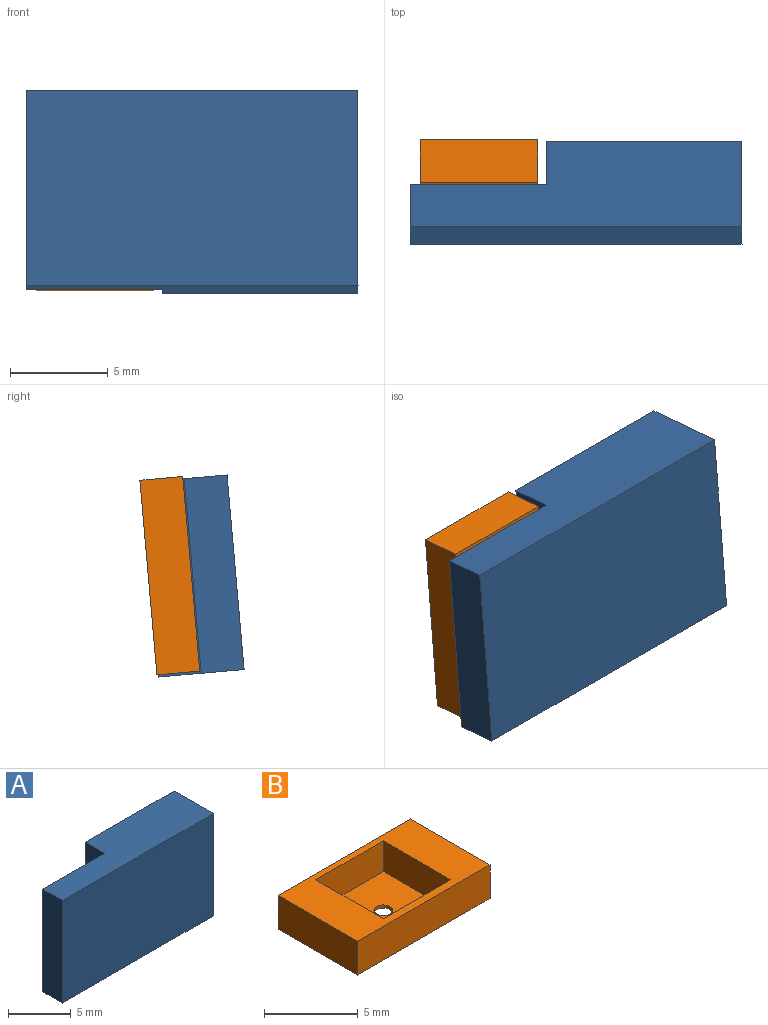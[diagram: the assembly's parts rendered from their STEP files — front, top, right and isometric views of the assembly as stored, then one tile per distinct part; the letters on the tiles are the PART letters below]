
ASSEMBLY  parts=2 mates=1
PART A: 13 faces, bbox 17x4.4x10 mm
  f0: plane 10x7mm, normal (0,1,0), area 44mm2, adj f1,f5,f6,f7,f8,f9,f10,f11
  f1: plane 10x2.2mm, normal (-1,0,0), area 22mm2, adj f0,f2,f6,f7
  f2: plane 17x10mm, normal (0,-1,0), area 170mm2, adj f1,f3,f6,f7
  f3: plane 10x4.4mm, normal (1,0,0), area 44mm2, adj f2,f4,f6,f7
  f4: plane 10x10mm, normal (0,1,0), area 100mm2, adj f3,f5,f6,f7
  f5: plane 10x2.2mm, normal (-1,0,0), area 22mm2, adj f0,f4,f6,f7
  f6: plane 17x4.4mm, normal (0,0,-1), area 59.4mm2, adj f0,f1,f2,f3,f4,f5
  f7: plane 17x4.4mm, normal (0,0,1), area 59.4mm2, adj f0,f1,f2,f3,f4,f5
  f8: plane 5.1x2mm, normal (0,0,-1), area 10.2mm2, adj f0,f9,f11,f12
  f9: plane 5.1x2mm, normal (-1,0,0), area 10.2mm2, adj f0,f8,f10,f12
  f10: plane 5.1x2mm, normal (0,0,1), area 10.2mm2, adj f0,f9,f11,f12
  f11: plane 5.1x2mm, normal (1,0,0), area 10.2mm2, adj f0,f8,f10,f12
  f12: plane 5.1x5.1mm, normal (0,1,0), area 26mm2, adj f8,f9,f10,f11
PART B: 12 faces, bbox 10x6x2.2 mm
  f0: plane 10x6mm, normal (0,0,1), area 34mm2, adj f1,f2,f3,f4,f6,f7,f8,f9
  f1: plane 6x2.2mm, normal (-1,0,0), area 13.2mm2, adj f0,f2,f4,f5
  f2: plane 10x2.2mm, normal (0,-1,0), area 22mm2, adj f0,f1,f3,f5
  f3: plane 6x2.2mm, normal (1,0,0), area 13.2mm2, adj f0,f2,f4,f5
  f4: plane 10x2.2mm, normal (0,1,0), area 22mm2, adj f0,f1,f3,f5
  f5: plane 10x6mm, normal (0,0,-1), area 59.2mm2, adj f1,f2,f3,f4,f11
  f6: plane 5.1x2mm, normal (1,0,0), area 10.2mm2, adj f0,f7,f9,f10
  f7: plane 5.1x2mm, normal (0,1,0), area 10.2mm2, adj f0,f6,f8,f10
  f8: plane 5.1x2mm, normal (-1,0,0), area 10.2mm2, adj f0,f7,f9,f10
  f9: plane 5.1x2mm, normal (0,-1,0), area 10.2mm2, adj f0,f6,f8,f10
  f10: plane 5.1x5.1mm, normal (0,0,1), area 25.2mm2, adj f6,f7,f8,f9,f11
  f11: cylinder r=0.5mm len=1mm, axis (0,0,1), area 0.6mm2, adj f5,f10
PLACE A rot(axis=(-1,0,0),5deg) t=(12.36,6.56,14.73)mm
PLACE B rot(axis=(0.56,-0.56,0.61),117.2deg) t=(18.89,7.96,4.69)mm
MATE parallel B.f0 <-> A.f12  axis (0,-1,0.09) through (15.89,7.96,4.69)mm
